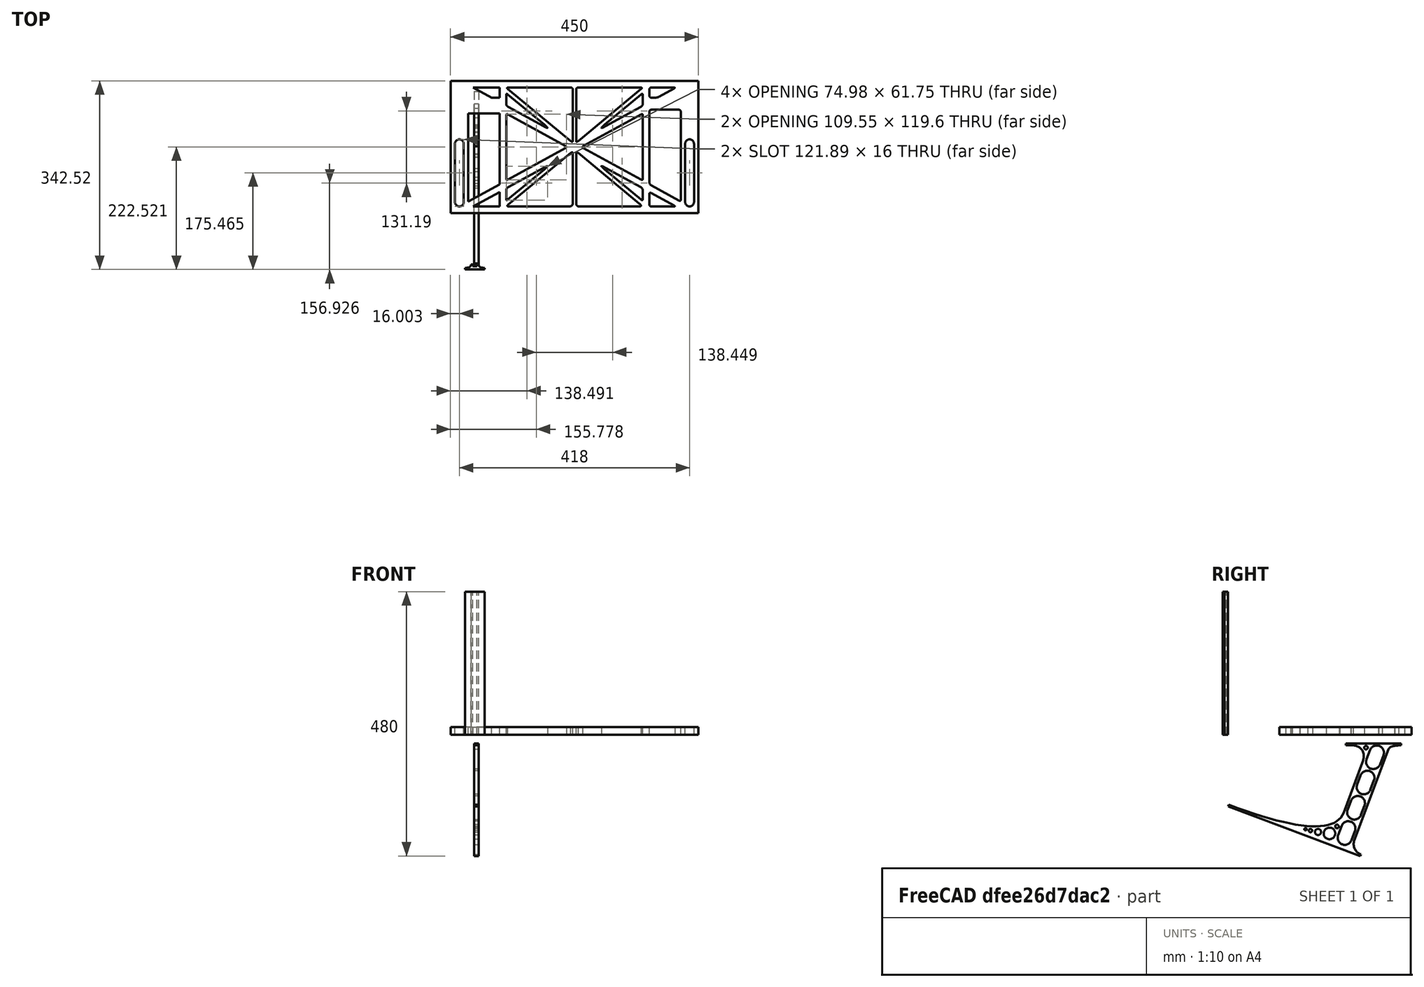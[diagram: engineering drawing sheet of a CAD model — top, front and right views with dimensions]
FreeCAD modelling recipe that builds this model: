
FCSTD DOCUMENT  (FreeCAD 0.19R0.19.2)
Label: laptopStand113
License: All rights reserved
LicenseURL: http://en.wikipedia.org/wiki/All_rights_reserved
objects: Sketcher::SketchObject×3, Part::Extrusion×3
note: 6 computed .brp shape members not serialized (recipe doc carries the construction recipe); baked Part::Feature solids carry a one-line shape summary decoded from their .brp

FEATURE [Sketcher::SketchObject] Sketch
  FullyConstrained = true
  sketch-geometry (310):
    g0: LineSegment StartX=-10.9272 StartY=-82.7794 StartZ=0 EndX=46.0728 EndY=-51.4823 EndZ=0
    g1: LineSegment StartX=-10.9272 StartY=77.3346 StartZ=0 EndX=-10.9272 EndY=-82.7794 EndZ=0
    g2: LineSegment StartX=-1.92719 StartY=-91.7794 StartZ=0 EndX=46.0728 EndY=-91.7794 EndZ=0
    g3: LineSegment StartX=46.0728 StartY=-65.424 StartZ=0 EndX=-1.92719 EndY=-91.7794 EndZ=0
    g4: LineSegment StartX=46.0728 StartY=-65.424 StartZ=0 EndX=46.0728 EndY=-91.7794 EndZ=0
    g5: LineSegment StartX=46.0728 StartY=77.3346 StartZ=0 EndX=46.0728 EndY=-51.4823 EndZ=0
    g6: LineSegment StartX=-42.9272 StartY=136.221 StartZ=0 EndX=-42.9272 EndY=-103.779 EndZ=0
    g7: LineSegment StartX=407.073 StartY=136.221 StartZ=0 EndX=407.073 EndY=-103.779 EndZ=0
    g8: ArcOfCircle CenterX=-26.9272 CenterY=22.1087 CenterZ=0 NormalX=0 NormalY=0 NormalZ=1 AngleXU=0 Radius=8 StartAngle=1e-16 EndAngle=3.14159
    g9: ArcOfCircle CenterX=-26.9272 CenterY=-83.7794 CenterZ=0 NormalX=0 NormalY=0 NormalZ=1 AngleXU=0 Radius=8 StartAngle=3.14159 EndAngle=6.28319
    g10: LineSegment StartX=-34.9272 StartY=22.1087 StartZ=0 EndX=-34.9272 EndY=-83.7794 EndZ=0
    g11: LineSegment StartX=-18.9272 StartY=22.1087 StartZ=0 EndX=-18.9272 EndY=-83.7794 EndZ=0
    g12: ArcOfCircle CenterX=391.073 CenterY=22.1087 CenterZ=0 NormalX=0 NormalY=0 NormalZ=1 AngleXU=0 Radius=8 StartAngle=-4.4e-15 EndAngle=3.14159
    g13: LineSegment StartX=399.073 StartY=22.1087 StartZ=0 EndX=399.073 EndY=-83.7794 EndZ=0
    g14: LineSegment StartX=383.073 StartY=22.1087 StartZ=0 EndX=383.073 EndY=-83.7794 EndZ=0
    g15: ArcOfCircle CenterX=391.073 CenterY=-83.7794 CenterZ=0 NormalX=0 NormalY=0 NormalZ=1 AngleXU=0 Radius=8 StartAngle=3.14159 EndAngle=6.28319
    g16: Circle CenterX=175.022 CenterY=27.0628 CenterZ=0 NormalX=0 NormalY=0 NormalZ=1 AngleXU=0 Radius=1
    g17: Circle CenterX=179.022 CenterY=24.8665 CenterZ=0 NormalX=0 NormalY=0 NormalZ=1 AngleXU=0 Radius=1
    g18: Circle CenterX=179.022 CenterY=27.0628 CenterZ=0 NormalX=0 NormalY=0 NormalZ=1 AngleXU=0 Radius=1
    g19: BSplineCurve PolesCount=3 KnotsCount=2 Degree=2 IsPeriodic=0
    g20: GeomPoint X=175.022 Y=27.0628 Z=0
    g21: GeomPoint X=179.022 Y=27.0628 Z=0
    g22: Circle CenterX=189.124 CenterY=27.0628 CenterZ=0 NormalX=0 NormalY=0 NormalZ=1 AngleXU=0 Radius=1
    g23: Circle CenterX=185.124 CenterY=24.8665 CenterZ=0 NormalX=0 NormalY=0 NormalZ=1 AngleXU=0 Radius=1
    g24: Circle CenterX=185.124 CenterY=27.0628 CenterZ=0 NormalX=0 NormalY=0 NormalZ=1 AngleXU=0 Radius=1
    g25: BSplineCurve PolesCount=3 KnotsCount=2 Degree=2 IsPeriodic=0
    g26: GeomPoint X=189.124 Y=27.0628 Z=0
    g27: GeomPoint X=185.124 Y=27.0628 Z=0
    g28: Circle CenterX=175.022 CenterY=5.37834 CenterZ=0 NormalX=0 NormalY=0 NormalZ=1 AngleXU=0 Radius=1
    g29: Circle CenterX=179.022 CenterY=7.57463 CenterZ=0 NormalX=0 NormalY=0 NormalZ=1 AngleXU=0 Radius=1
    g30: Circle CenterX=179.022 CenterY=5.34704 CenterZ=0 NormalX=0 NormalY=0 NormalZ=1 AngleXU=0 Radius=1
    g31: BSplineCurve PolesCount=3 KnotsCount=2 Degree=2 IsPeriodic=0
    g32: GeomPoint X=175.022 Y=5.37834 Z=0
    g33: GeomPoint X=179.022 Y=5.34704 Z=0
    g34: Circle CenterX=189.124 CenterY=5.37834 CenterZ=0 NormalX=0 NormalY=0 NormalZ=1 AngleXU=0 Radius=1
    g35: Circle CenterX=185.124 CenterY=7.57463 CenterZ=0 NormalX=0 NormalY=0 NormalZ=1 AngleXU=0 Radius=1
    g36: Circle CenterX=185.124 CenterY=5.34704 CenterZ=0 NormalX=0 NormalY=0 NormalZ=1 AngleXU=0 Radius=1
    g37: BSplineCurve PolesCount=3 KnotsCount=2 Degree=2 IsPeriodic=0
    g38: GeomPoint X=189.124 Y=5.37834 Z=0
    g39: GeomPoint X=185.124 Y=5.34704 Z=0
    g40: Circle CenterX=165.871 CenterY=18.1458 CenterZ=0 NormalX=0 NormalY=0 NormalZ=1 AngleXU=0 Radius=1
    g41: Circle CenterX=169.377 CenterY=16.2206 CenterZ=0 NormalX=0 NormalY=0 NormalZ=1 AngleXU=0 Radius=1
    g42: Circle CenterX=165.871 CenterY=14.2954 CenterZ=0 NormalX=0 NormalY=0 NormalZ=1 AngleXU=0 Radius=1
    g43: BSplineCurve PolesCount=3 KnotsCount=2 Degree=2 IsPeriodic=0
    g44: GeomPoint X=165.871 Y=18.1458 Z=0
    g45: GeomPoint X=165.871 Y=14.2954 Z=0
    g46: Circle CenterX=198.275 CenterY=18.1458 CenterZ=0 NormalX=0 NormalY=0 NormalZ=1 AngleXU=0 Radius=1
    g47: Circle CenterX=194.768 CenterY=16.2206 CenterZ=0 NormalX=0 NormalY=0 NormalZ=1 AngleXU=0 Radius=1
    g48: Circle CenterX=198.275 CenterY=14.2954 CenterZ=0 NormalX=0 NormalY=0 NormalZ=1 AngleXU=0 Radius=1
    g49: BSplineCurve PolesCount=3 KnotsCount=2 Degree=2 IsPeriodic=0
    g50: GeomPoint X=198.275 Y=18.1458 Z=0
    g51: GeomPoint X=198.275 Y=14.2954 Z=0
    g52: LineSegment StartX=407.073 StartY=-103.779 StartZ=0 EndX=-42.9272 EndY=-103.779 EndZ=0
    g53: LineSegment StartX=407.073 StartY=136.221 StartZ=0 EndX=-42.9272 EndY=136.221 EndZ=0
    g54: LineSegment StartX=46.0728 StartY=77.3346 StartZ=0 EndX=-10.9272 EndY=77.3346 EndZ=0
    g55: LineSegment StartX=46.0728 StartY=105.865 StartZ=0 EndX=31.5028 EndY=105.865 EndZ=0
    g56: LineSegment StartX=46.0728 StartY=124.221 StartZ=0 EndX=46.0728 EndY=105.865 EndZ=0
    g57: LineSegment StartX=-1.92719 StartY=124.221 StartZ=0 EndX=31.5028 EndY=105.865 EndZ=0
    g58: LineSegment StartX=46.0728 StartY=124.221 StartZ=0 EndX=-1.92719 EndY=124.221 EndZ=0
    g59: Circle CenterX=125.607 CenterY=54.1951 CenterZ=0 NormalX=0 NormalY=0 NormalZ=1 AngleXU=0 Radius=1
    g60: Circle CenterX=139.632 CenterY=46.4944 CenterZ=0 NormalX=0 NormalY=0 NormalZ=1 AngleXU=0 Radius=1
    g61: Circle CenterX=127.326 CenterY=56.7187 CenterZ=0 NormalX=0 NormalY=0 NormalZ=1 AngleXU=0 Radius=1
    g62: BSplineCurve PolesCount=3 KnotsCount=2 Degree=2 IsPeriodic=0
    g63: GeomPoint X=125.607 Y=54.1951 Z=0
    g64: GeomPoint X=127.326 Y=56.7187 Z=0
    g65: Circle CenterX=236.821 CenterY=56.7187 CenterZ=0 NormalX=0 NormalY=0 NormalZ=1 AngleXU=0 Radius=1
    g66: Circle CenterX=224.513 CenterY=46.4944 CenterZ=0 NormalX=0 NormalY=0 NormalZ=1 AngleXU=0 Radius=1
    g67: Circle CenterX=238.538 CenterY=54.1951 CenterZ=0 NormalX=0 NormalY=0 NormalZ=1 AngleXU=0 Radius=1
    g68: BSplineCurve PolesCount=3 KnotsCount=2 Degree=2 IsPeriodic=0
    g69: GeomPoint X=236.821 Y=56.7187 Z=0
    g70: GeomPoint X=238.538 Y=54.1951 Z=0
    g71: Circle CenterX=238.538 CenterY=-21.7539 CenterZ=0 NormalX=0 NormalY=0 NormalZ=1 AngleXU=0 Radius=1
    g72: Circle CenterX=224.513 CenterY=-14.0532 CenterZ=0 NormalX=0 NormalY=0 NormalZ=1 AngleXU=0 Radius=1
    g73: Circle CenterX=236.821 CenterY=-24.2775 CenterZ=0 NormalX=0 NormalY=0 NormalZ=1 AngleXU=0 Radius=1
    g74: BSplineCurve PolesCount=3 KnotsCount=2 Degree=2 IsPeriodic=0
    g75: GeomPoint X=238.538 Y=-21.7539 Z=0
    g76: GeomPoint X=236.821 Y=-24.2775 Z=0
    g77: Circle CenterX=125.607 CenterY=-21.7539 CenterZ=0 NormalX=0 NormalY=0 NormalZ=1 AngleXU=0 Radius=1
    g78: Circle CenterX=139.632 CenterY=-14.0532 CenterZ=0 NormalX=0 NormalY=0 NormalZ=1 AngleXU=0 Radius=1
    g79: Circle CenterX=127.325 CenterY=-24.2775 CenterZ=0 NormalX=0 NormalY=0 NormalZ=1 AngleXU=0 Radius=1
    g80: BSplineCurve PolesCount=3 KnotsCount=2 Degree=2 IsPeriodic=0
    g81: GeomPoint X=125.607 Y=-21.7539 Z=0
    g82: GeomPoint X=127.325 Y=-24.2775 Z=0
    g83: Circle CenterX=302.996 CenterY=111.695 CenterZ=0 NormalX=0 NormalY=0 NormalZ=1 AngleXU=0 Radius=1
    g84: Circle CenterX=306.073 CenterY=114.251 CenterZ=0 NormalX=0 NormalY=0 NormalZ=1 AngleXU=0 Radius=1
    g85: Circle CenterX=306.073 CenterY=110.251 CenterZ=0 NormalX=0 NormalY=0 NormalZ=1 AngleXU=0 Radius=1
    g86: BSplineCurve PolesCount=3 KnotsCount=2 Degree=2 IsPeriodic=0
    g87: GeomPoint X=302.996 Y=111.695 Z=0
    g88: GeomPoint X=306.073 Y=110.251 Z=0
    g89: Circle CenterX=306.073 CenterY=95.2763 CenterZ=0 NormalX=0 NormalY=0 NormalZ=1 AngleXU=0 Radius=1
    g90: Circle CenterX=306.073 CenterY=91.2763 CenterZ=0 NormalX=0 NormalY=0 NormalZ=1 AngleXU=0 Radius=1
    g91: Circle CenterX=302.567 CenterY=89.3511 CenterZ=0 NormalX=0 NormalY=0 NormalZ=1 AngleXU=0 Radius=1
    g92: BSplineCurve PolesCount=3 KnotsCount=2 Degree=2 IsPeriodic=0
    g93: GeomPoint X=306.073 Y=95.2763 Z=0
    g94: GeomPoint X=302.567 Y=89.3511 Z=0
    g95: LineSegment StartX=306.073 StartY=110.251 StartZ=0 EndX=306.073 EndY=95.2763 EndZ=0
    g96: LineSegment StartX=302.996 StartY=111.695 StartZ=0 EndX=236.821 EndY=56.7187 EndZ=0
    g97: LineSegment StartX=238.538 StartY=54.1951 StartZ=0 EndX=302.567 EndY=89.3511 EndZ=0
    g98: Circle CenterX=61.1496 CenterY=111.695 CenterZ=0 NormalX=0 NormalY=0 NormalZ=1 AngleXU=0 Radius=1
    g99: Circle CenterX=58.0728 CenterY=114.251 CenterZ=0 NormalX=0 NormalY=0 NormalZ=1 AngleXU=0 Radius=1
    g100: Circle CenterX=58.0728 CenterY=110.251 CenterZ=0 NormalX=0 NormalY=0 NormalZ=1 AngleXU=0 Radius=1
    g101: BSplineCurve PolesCount=3 KnotsCount=2 Degree=2 IsPeriodic=0
    g102: GeomPoint X=61.1496 Y=111.695 Z=0
    g103: GeomPoint X=58.0728 Y=110.251 Z=0
    g104: Circle CenterX=61.5791 CenterY=89.3511 CenterZ=0 NormalX=0 NormalY=0 NormalZ=1 AngleXU=0 Radius=1
    g105: Circle CenterX=58.0728 CenterY=91.2763 CenterZ=0 NormalX=0 NormalY=0 NormalZ=1 AngleXU=0 Radius=1
    g106: Circle CenterX=58.0728 CenterY=95.2763 CenterZ=0 NormalX=0 NormalY=0 NormalZ=1 AngleXU=0 Radius=1
    g107: BSplineCurve PolesCount=3 KnotsCount=2 Degree=2 IsPeriodic=0
    g108: GeomPoint X=61.5791 Y=89.3511 Z=0
    g109: GeomPoint X=58.0728 Y=95.2763 Z=0
    g110: LineSegment StartX=58.0728 StartY=110.251 StartZ=0 EndX=58.0728 EndY=95.2763 EndZ=0
    g111: LineSegment StartX=61.1496 StartY=111.695 StartZ=0 EndX=127.326 EndY=56.7187 EndZ=0
    g112: LineSegment StartX=125.607 StartY=54.1951 StartZ=0 EndX=61.5791 EndY=89.3511 EndZ=0
    g113: Circle CenterX=61.5791 CenterY=-56.9099 CenterZ=0 NormalX=0 NormalY=0 NormalZ=1 AngleXU=0 Radius=1
    g114: Circle CenterX=58.0728 CenterY=-58.8351 CenterZ=0 NormalX=0 NormalY=0 NormalZ=1 AngleXU=0 Radius=1
    g115: Circle CenterX=58.0728 CenterY=-62.8351 CenterZ=0 NormalX=0 NormalY=0 NormalZ=1 AngleXU=0 Radius=1
    g116: BSplineCurve PolesCount=3 KnotsCount=2 Degree=2 IsPeriodic=0
    g117: GeomPoint X=61.5791 Y=-56.9099 Z=0
    g118: GeomPoint X=58.0728 Y=-62.8351 Z=0
    g119: Circle CenterX=58.0728 CenterY=-77.8102 CenterZ=0 NormalX=0 NormalY=0 NormalZ=1 AngleXU=0 Radius=1
    g120: Circle CenterX=58.0728 CenterY=-81.8102 CenterZ=0 NormalX=0 NormalY=0 NormalZ=1 AngleXU=0 Radius=1
    g121: Circle CenterX=61.1496 CenterY=-79.2541 CenterZ=0 NormalX=0 NormalY=0 NormalZ=1 AngleXU=0 Radius=1
    g122: BSplineCurve PolesCount=3 KnotsCount=2 Degree=2 IsPeriodic=0
    g123: GeomPoint X=58.0728 Y=-77.8102 Z=0
    g124: GeomPoint X=61.1496 Y=-79.2541 Z=0
    g125: LineSegment StartX=58.0728 StartY=-62.8351 StartZ=0 EndX=58.0728 EndY=-77.8102 EndZ=0
    g126: LineSegment StartX=61.1496 StartY=-79.2541 StartZ=0 EndX=127.325 EndY=-24.2775 EndZ=0
    g127: LineSegment StartX=125.607 StartY=-21.7539 StartZ=0 EndX=61.5791 EndY=-56.9099 EndZ=0
    g128: Circle CenterX=302.567 CenterY=-56.9099 CenterZ=0 NormalX=0 NormalY=0 NormalZ=1 AngleXU=0 Radius=1
    g129: Circle CenterX=306.073 CenterY=-58.8351 CenterZ=0 NormalX=0 NormalY=0 NormalZ=1 AngleXU=0 Radius=1
    g130: Circle CenterX=306.073 CenterY=-62.8351 CenterZ=0 NormalX=0 NormalY=0 NormalZ=1 AngleXU=0 Radius=1
    g131: BSplineCurve PolesCount=3 KnotsCount=2 Degree=2 IsPeriodic=0
    g132: GeomPoint X=302.567 Y=-56.9099 Z=0
    g133: GeomPoint X=306.073 Y=-62.8351 Z=0
    g134: Circle CenterX=302.996 CenterY=-79.2541 CenterZ=0 NormalX=0 NormalY=0 NormalZ=1 AngleXU=0 Radius=1
    g135: Circle CenterX=306.073 CenterY=-81.8102 CenterZ=0 NormalX=0 NormalY=0 NormalZ=1 AngleXU=0 Radius=1
    g136: Circle CenterX=306.073 CenterY=-77.8102 CenterZ=0 NormalX=0 NormalY=0 NormalZ=1 AngleXU=0 Radius=1
    g137: BSplineCurve PolesCount=3 KnotsCount=2 Degree=2 IsPeriodic=0
    g138: GeomPoint X=302.996 Y=-79.2541 Z=0
    g139: GeomPoint X=306.073 Y=-77.8102 Z=0
    g140: LineSegment StartX=306.073 StartY=-62.8351 StartZ=0 EndX=306.073 EndY=-77.8102 EndZ=0
    g141: LineSegment StartX=302.996 StartY=-79.2541 StartZ=0 EndX=236.821 EndY=-24.2775 EndZ=0
    g142: LineSegment StartX=238.538 StartY=-21.7539 StartZ=0 EndX=302.567 EndY=-56.9099 EndZ=0
    g143: Circle CenterX=61.6457 CenterY=-88.8112 CenterZ=0 NormalX=0 NormalY=0 NormalZ=1 AngleXU=0 Radius=1
    g144: Circle CenterX=58.0728 CenterY=-91.7794 CenterZ=0 NormalX=0 NormalY=0 NormalZ=1 AngleXU=0 Radius=1
    g145: Circle CenterX=63.9135 CenterY=-91.7794 CenterZ=0 NormalX=0 NormalY=0 NormalZ=1 AngleXU=0 Radius=1
    g146: BSplineCurve PolesCount=3 KnotsCount=2 Degree=2 IsPeriodic=0
    g147: GeomPoint X=61.6457 Y=-88.8112 Z=0
    g148: GeomPoint X=63.9135 Y=-91.7794 Z=0
    g149: Circle CenterX=179.022 CenterY=-85.8163 CenterZ=0 NormalX=0 NormalY=0 NormalZ=1 AngleXU=0 Radius=1
    g150: Circle CenterX=179.022 CenterY=-91.7794 CenterZ=0 NormalX=0 NormalY=0 NormalZ=1 AngleXU=0 Radius=1
    g151: Circle CenterX=171.895 CenterY=-91.7794 CenterZ=0 NormalX=0 NormalY=0 NormalZ=1 AngleXU=0 Radius=1
    g152: BSplineCurve PolesCount=3 KnotsCount=2 Degree=2 IsPeriodic=0
    g153: GeomPoint X=179.022 Y=-85.8163 Z=0
    g154: GeomPoint X=171.895 Y=-91.7794 Z=0
    g155: Circle CenterX=185.124 CenterY=-86.2028 CenterZ=0 NormalX=0 NormalY=0 NormalZ=1 AngleXU=0 Radius=1
    g156: Circle CenterX=185.124 CenterY=-91.7794 CenterZ=0 NormalX=0 NormalY=0 NormalZ=1 AngleXU=0 Radius=1
    g157: Circle CenterX=191.747 CenterY=-91.7794 CenterZ=0 NormalX=0 NormalY=0 NormalZ=1 AngleXU=0 Radius=1
    g158: BSplineCurve PolesCount=3 KnotsCount=2 Degree=2 IsPeriodic=0
    g159: GeomPoint X=185.124 Y=-86.2028 Z=0
    g160: GeomPoint X=191.747 Y=-91.7794 Z=0
    g161: Circle CenterX=299.888 CenterY=-86.6413 CenterZ=0 NormalX=0 NormalY=0 NormalZ=1 AngleXU=0 Radius=1
    g162: Circle CenterX=306.073 CenterY=-91.7794 CenterZ=0 NormalX=0 NormalY=0 NormalZ=1 AngleXU=0 Radius=1
    g163: Circle CenterX=298.776 CenterY=-91.7794 CenterZ=0 NormalX=0 NormalY=0 NormalZ=1 AngleXU=0 Radius=1
    g164: BSplineCurve PolesCount=3 KnotsCount=2 Degree=2 IsPeriodic=0
    g165: GeomPoint X=299.888 Y=-86.6413 Z=0
    g166: GeomPoint X=298.776 Y=-91.7794 Z=0
    g167: LineSegment StartX=189.124 StartY=5.37834 StartZ=0 EndX=299.888 EndY=-86.6413 EndZ=0
    g168: LineSegment StartX=298.776 StartY=-91.7794 StartZ=0 EndX=191.747 EndY=-91.7794 EndZ=0
    g169: LineSegment StartX=185.124 StartY=-86.2028 StartZ=0 EndX=185.124 EndY=5.34704 EndZ=0
    g170: LineSegment StartX=179.022 StartY=5.34704 StartZ=0 EndX=179.022 EndY=-85.8163 EndZ=0
    g171: LineSegment StartX=171.895 StartY=-91.7794 StartZ=0 EndX=63.9135 EndY=-91.7794 EndZ=0
    g172: LineSegment StartX=61.6457 StartY=-88.8112 StartZ=0 EndX=175.022 EndY=5.37834 EndZ=0
    g173: Circle CenterX=302.073 CenterY=124.221 CenterZ=0 NormalX=0 NormalY=0 NormalZ=1 AngleXU=0 Radius=1
    g174: Circle CenterX=306.073 CenterY=124.221 CenterZ=0 NormalX=0 NormalY=0 NormalZ=1 AngleXU=0 Radius=1
    g175: Circle CenterX=302.996 CenterY=121.665 CenterZ=0 NormalX=0 NormalY=0 NormalZ=1 AngleXU=0 Radius=1
    g176: BSplineCurve PolesCount=3 KnotsCount=2 Degree=2 IsPeriodic=0
    g177: GeomPoint X=302.073 Y=124.221 Z=0
    g178: GeomPoint X=302.996 Y=121.665 Z=0
    g179: Circle CenterX=189.124 CenterY=124.221 CenterZ=0 NormalX=0 NormalY=0 NormalZ=1 AngleXU=0 Radius=1
    g180: Circle CenterX=185.124 CenterY=124.221 CenterZ=0 NormalX=0 NormalY=0 NormalZ=1 AngleXU=0 Radius=1
    g181: Circle CenterX=185.124 CenterY=120.221 CenterZ=0 NormalX=0 NormalY=0 NormalZ=1 AngleXU=0 Radius=1
    g182: BSplineCurve PolesCount=3 KnotsCount=2 Degree=2 IsPeriodic=0
    g183: GeomPoint X=189.124 Y=124.221 Z=0
    g184: GeomPoint X=185.124 Y=120.221 Z=0
    g185: Circle CenterX=175.022 CenterY=124.221 CenterZ=0 NormalX=0 NormalY=0 NormalZ=1 AngleXU=0 Radius=1
    g186: Circle CenterX=179.022 CenterY=124.221 CenterZ=0 NormalX=0 NormalY=0 NormalZ=1 AngleXU=0 Radius=1
    g187: Circle CenterX=179.022 CenterY=120.221 CenterZ=0 NormalX=0 NormalY=0 NormalZ=1 AngleXU=0 Radius=1
    g188: BSplineCurve PolesCount=3 KnotsCount=2 Degree=2 IsPeriodic=0
    g189: GeomPoint X=175.022 Y=124.221 Z=0
    g190: GeomPoint X=179.022 Y=120.221 Z=0
    g191: Circle CenterX=62.0728 CenterY=124.221 CenterZ=0 NormalX=0 NormalY=0 NormalZ=1 AngleXU=0 Radius=1
    g192: Circle CenterX=58.0728 CenterY=124.221 CenterZ=0 NormalX=0 NormalY=0 NormalZ=1 AngleXU=0 Radius=1
    g193: Circle CenterX=61.1496 CenterY=121.665 CenterZ=0 NormalX=0 NormalY=0 NormalZ=1 AngleXU=0 Radius=1
    g194: BSplineCurve PolesCount=3 KnotsCount=2 Degree=2 IsPeriodic=0
    g195: GeomPoint X=62.0728 Y=124.221 Z=0
    g196: GeomPoint X=61.1496 Y=121.665 Z=0
    g197: LineSegment StartX=62.0728 StartY=124.221 StartZ=0 EndX=175.022 EndY=124.221 EndZ=0
    g198: LineSegment StartX=179.022 StartY=120.221 StartZ=0 EndX=179.022 EndY=27.0628 EndZ=0
    g199: LineSegment StartX=185.124 StartY=27.0628 StartZ=0 EndX=185.124 EndY=120.221 EndZ=0
    g200: LineSegment StartX=189.124 StartY=124.221 StartZ=0 EndX=302.073 EndY=124.221 EndZ=0
    g201: LineSegment StartX=302.996 StartY=121.665 StartZ=0 EndX=189.124 EndY=27.0628 EndZ=0
    g202: LineSegment StartX=175.022 StartY=27.0628 StartZ=0 EndX=61.1496 EndY=121.665 EndZ=0
    g203: Circle CenterX=61.5791 CenterY=75.4095 CenterZ=0 NormalX=0 NormalY=0 NormalZ=1 AngleXU=0 Radius=1
    g204: Circle CenterX=58.0728 CenterY=77.3346 CenterZ=0 NormalX=0 NormalY=0 NormalZ=1 AngleXU=0 Radius=1
    g205: Circle CenterX=58.0728 CenterY=73.3346 CenterZ=0 NormalX=0 NormalY=0 NormalZ=1 AngleXU=0 Radius=1
    g206: BSplineCurve PolesCount=3 KnotsCount=2 Degree=2 IsPeriodic=0
    g207: GeomPoint X=61.5791 Y=75.4095 Z=0
    g208: GeomPoint X=58.0728 Y=73.3346 Z=0
    g209: Circle CenterX=58.0728 CenterY=-40.8935 CenterZ=0 NormalX=0 NormalY=0 NormalZ=1 AngleXU=0 Radius=1
    g210: Circle CenterX=58.0728 CenterY=-44.8935 CenterZ=0 NormalX=0 NormalY=0 NormalZ=1 AngleXU=0 Radius=1
    g211: Circle CenterX=61.5791 CenterY=-42.9683 CenterZ=0 NormalX=0 NormalY=0 NormalZ=1 AngleXU=0 Radius=1
    g212: BSplineCurve PolesCount=3 KnotsCount=2 Degree=2 IsPeriodic=0
    g213: GeomPoint X=58.0728 Y=-40.8935 Z=0
    g214: GeomPoint X=61.5791 Y=-42.9683 Z=0
    g215: LineSegment StartX=61.5791 StartY=-42.9683 StartZ=0 EndX=165.871 EndY=14.2954 EndZ=0
    g216: LineSegment StartX=165.871 StartY=18.1458 StartZ=0 EndX=61.5791 EndY=75.4095 EndZ=0
    g217: LineSegment StartX=58.0728 StartY=73.3346 StartZ=0 EndX=58.0728 EndY=-40.8935 EndZ=0
    g218: Circle CenterX=302.567 CenterY=-42.9683 CenterZ=0 NormalX=0 NormalY=0 NormalZ=1 AngleXU=0 Radius=1
    g219: Circle CenterX=306.073 CenterY=-44.8935 CenterZ=0 NormalX=0 NormalY=0 NormalZ=1 AngleXU=0 Radius=1
    g220: Circle CenterX=306.073 CenterY=-40.8935 CenterZ=0 NormalX=0 NormalY=0 NormalZ=1 AngleXU=0 Radius=1
    g221: BSplineCurve PolesCount=3 KnotsCount=2 Degree=2 IsPeriodic=0
    g222: GeomPoint X=302.567 Y=-42.9683 Z=0
    g223: GeomPoint X=306.073 Y=-40.8935 Z=0
    g224: Circle CenterX=306.073 CenterY=73.3346 CenterZ=0 NormalX=0 NormalY=0 NormalZ=1 AngleXU=0 Radius=1
    g225: Circle CenterX=306.073 CenterY=77.3346 CenterZ=0 NormalX=0 NormalY=0 NormalZ=1 AngleXU=0 Radius=1
    g226: Circle CenterX=302.567 CenterY=75.4095 CenterZ=0 NormalX=0 NormalY=0 NormalZ=1 AngleXU=0 Radius=1
    g227: BSplineCurve PolesCount=3 KnotsCount=2 Degree=2 IsPeriodic=0
    g228: GeomPoint X=306.073 Y=73.3346 Z=0
    g229: GeomPoint X=302.567 Y=75.4095 Z=0
    g230: LineSegment StartX=302.567 StartY=-42.9683 StartZ=0 EndX=198.275 EndY=14.2954 EndZ=0
    g231: LineSegment StartX=198.275 StartY=18.1458 StartZ=0 EndX=302.567 EndY=75.4095 EndZ=0
    g232: LineSegment StartX=306.073 StartY=73.3346 StartZ=0 EndX=306.073 EndY=-40.8935 EndZ=0
    g233: LineSegment StartX=322.073 StartY=105.865 StartZ=0 EndX=328.643 EndY=105.865 EndZ=0
    g234: LineSegment StartX=318.073 StartY=120.221 StartZ=0 EndX=318.073 EndY=109.865 EndZ=0
    g235: LineSegment StartX=336.157 StartY=107.779 StartZ=0 EndX=362.567 EndY=122.294 EndZ=0
    g236: Circle CenterX=362.073 CenterY=124.221 CenterZ=0 NormalX=0 NormalY=0 NormalZ=1 AngleXU=0 Radius=1
    g237: Circle CenterX=366.073 CenterY=124.221 CenterZ=0 NormalX=0 NormalY=0 NormalZ=1 AngleXU=0 Radius=1
    g238: Circle CenterX=362.567 CenterY=122.294 CenterZ=0 NormalX=0 NormalY=0 NormalZ=1 AngleXU=0 Radius=1
    g239: BSplineCurve PolesCount=3 KnotsCount=2 Degree=2 IsPeriodic=0
    g240: GeomPoint X=362.073 Y=124.221 Z=0
    g241: GeomPoint X=362.567 Y=122.294 Z=0
    g242: Circle CenterX=322.073 CenterY=124.221 CenterZ=0 NormalX=0 NormalY=0 NormalZ=1 AngleXU=0 Radius=1
    g243: Circle CenterX=318.073 CenterY=124.221 CenterZ=0 NormalX=0 NormalY=0 NormalZ=1 AngleXU=0 Radius=1
    g244: Circle CenterX=318.073 CenterY=120.221 CenterZ=0 NormalX=0 NormalY=0 NormalZ=1 AngleXU=0 Radius=1
    g245: BSplineCurve PolesCount=3 KnotsCount=2 Degree=2 IsPeriodic=0
    g246: GeomPoint X=322.073 Y=124.221 Z=0
    g247: GeomPoint X=318.073 Y=120.221 Z=0
    g248: Circle CenterX=322.073 CenterY=105.865 CenterZ=0 NormalX=0 NormalY=0 NormalZ=1 AngleXU=0 Radius=1
    g249: Circle CenterX=318.073 CenterY=105.865 CenterZ=0 NormalX=0 NormalY=0 NormalZ=1 AngleXU=0 Radius=1
    g250: Circle CenterX=318.073 CenterY=109.865 CenterZ=0 NormalX=0 NormalY=0 NormalZ=1 AngleXU=0 Radius=1
    g251: BSplineCurve PolesCount=3 KnotsCount=2 Degree=2 IsPeriodic=0
    g252: GeomPoint X=322.073 Y=105.865 Z=0
    g253: GeomPoint X=318.073 Y=109.865 Z=0
    g254: Circle CenterX=336.157 CenterY=107.779 CenterZ=0 NormalX=0 NormalY=0 NormalZ=1 AngleXU=0 Radius=1
    g255: Circle CenterX=332.651 CenterY=105.853 CenterZ=0 NormalX=0 NormalY=0 NormalZ=1 AngleXU=0 Radius=1
    g256: Circle CenterX=328.643 CenterY=105.865 CenterZ=0 NormalX=0 NormalY=0 NormalZ=1 AngleXU=0 Radius=1
    g257: BSplineCurve PolesCount=3 KnotsCount=2 Degree=2 IsPeriodic=0
    g258: GeomPoint X=336.157 Y=107.779 Z=0
    g259: GeomPoint X=328.643 Y=105.865 Z=0
    g260: LineSegment StartX=322.073 StartY=124.221 StartZ=0 EndX=362.073 EndY=124.221 EndZ=0
    g261: Circle CenterX=371.567 CenterY=-80.8644 CenterZ=0 NormalX=0 NormalY=0 NormalZ=1 AngleXU=0 Radius=1
    g262: Circle CenterX=375.073 CenterY=-82.7896 CenterZ=0 NormalX=0 NormalY=0 NormalZ=1 AngleXU=0 Radius=1
    g263: Circle CenterX=375.073 CenterY=-78.7896 CenterZ=0 NormalX=0 NormalY=0 NormalZ=1 AngleXU=0 Radius=1
    g264: BSplineCurve PolesCount=3 KnotsCount=2 Degree=2 IsPeriodic=0
    g265: GeomPoint X=371.567 Y=-80.8644 Z=0
    g266: GeomPoint X=375.073 Y=-78.7896 Z=0
    g267: Circle CenterX=321.579 CenterY=-53.4075 CenterZ=0 NormalX=0 NormalY=0 NormalZ=1 AngleXU=0 Radius=1
    g268: Circle CenterX=318.073 CenterY=-51.4823 CenterZ=0 NormalX=0 NormalY=0 NormalZ=1 AngleXU=0 Radius=1
    g269: Circle CenterX=318.073 CenterY=-47.4823 CenterZ=0 NormalX=0 NormalY=0 NormalZ=1 AngleXU=0 Radius=1
    g270: BSplineCurve PolesCount=3 KnotsCount=2 Degree=2 IsPeriodic=0
    g271: GeomPoint X=321.579 Y=-53.4075 Z=0
    g272: GeomPoint X=318.073 Y=-47.4823 Z=0
    g273: Circle CenterX=318.073 CenterY=79.9235 CenterZ=0 NormalX=0 NormalY=0 NormalZ=1 AngleXU=0 Radius=1
    g274: Circle CenterX=318.073 CenterY=83.9235 CenterZ=0 NormalX=0 NormalY=0 NormalZ=1 AngleXU=0 Radius=1
    g275: Circle CenterX=322.073 CenterY=83.9235 CenterZ=0 NormalX=0 NormalY=0 NormalZ=1 AngleXU=0 Radius=1
    g276: BSplineCurve PolesCount=3 KnotsCount=2 Degree=2 IsPeriodic=0
    g277: GeomPoint X=318.073 Y=79.9235 Z=0
    g278: GeomPoint X=322.073 Y=83.9235 Z=0
    g279: Circle CenterX=375.073 CenterY=79.9235 CenterZ=0 NormalX=0 NormalY=0 NormalZ=1 AngleXU=0 Radius=1
    g280: Circle CenterX=375.073 CenterY=83.9235 CenterZ=0 NormalX=0 NormalY=0 NormalZ=1 AngleXU=0 Radius=1
    g281: Circle CenterX=371.073 CenterY=83.9235 CenterZ=0 NormalX=0 NormalY=0 NormalZ=1 AngleXU=0 Radius=1
    g282: BSplineCurve PolesCount=3 KnotsCount=2 Degree=2 IsPeriodic=0
    g283: GeomPoint X=375.073 Y=79.9235 Z=0
    g284: GeomPoint X=371.073 Y=83.9235 Z=0
    g285: LineSegment StartX=322.073 StartY=83.9235 StartZ=0 EndX=371.073 EndY=83.9235 EndZ=0
    g286: LineSegment StartX=375.073 StartY=79.9235 StartZ=0 EndX=375.073 EndY=-78.7896 EndZ=0
    g287: LineSegment StartX=371.567 StartY=-80.8644 StartZ=0 EndX=321.579 EndY=-53.4075 EndZ=0
    g288: LineSegment StartX=318.073 StartY=-47.4823 StartZ=0 EndX=318.073 EndY=79.9235 EndZ=0
    g289: Circle CenterX=321.579 CenterY=-67.3492 CenterZ=0 NormalX=0 NormalY=0 NormalZ=1 AngleXU=0 Radius=1
    g290: Circle CenterX=318.073 CenterY=-65.424 CenterZ=0 NormalX=0 NormalY=0 NormalZ=1 AngleXU=0 Radius=1
    g291: Circle CenterX=318.073 CenterY=-69.424 CenterZ=0 NormalX=0 NormalY=0 NormalZ=1 AngleXU=0 Radius=1
    g292: BSplineCurve PolesCount=3 KnotsCount=2 Degree=2 IsPeriodic=0
    g293: GeomPoint X=321.579 Y=-67.3492 Z=0
    g294: GeomPoint X=318.073 Y=-69.424 Z=0
    g295: Circle CenterX=362.567 CenterY=-89.8542 CenterZ=0 NormalX=0 NormalY=0 NormalZ=1 AngleXU=0 Radius=1
    g296: Circle CenterX=366.073 CenterY=-91.7794 CenterZ=0 NormalX=0 NormalY=0 NormalZ=1 AngleXU=0 Radius=1
    g297: Circle CenterX=362.073 CenterY=-91.7794 CenterZ=0 NormalX=0 NormalY=0 NormalZ=1 AngleXU=0 Radius=1
    g298: BSplineCurve PolesCount=3 KnotsCount=2 Degree=2 IsPeriodic=0
    g299: GeomPoint X=362.567 Y=-89.8542 Z=0
    g300: GeomPoint X=362.073 Y=-91.7794 Z=0
    g301: Circle CenterX=322.073 CenterY=-91.7794 CenterZ=0 NormalX=0 NormalY=0 NormalZ=1 AngleXU=0 Radius=1
    g302: Circle CenterX=318.073 CenterY=-91.7794 CenterZ=0 NormalX=0 NormalY=0 NormalZ=1 AngleXU=0 Radius=1
    g303: Circle CenterX=318.073 CenterY=-87.7794 CenterZ=0 NormalX=0 NormalY=0 NormalZ=1 AngleXU=0 Radius=1
    g304: BSplineCurve PolesCount=3 KnotsCount=2 Degree=2 IsPeriodic=0
    g305: GeomPoint X=322.073 Y=-91.7794 Z=0
    g306: GeomPoint X=318.073 Y=-87.7794 Z=0
    g307: LineSegment StartX=362.567 StartY=-89.8542 StartZ=0 EndX=321.579 EndY=-67.3492 EndZ=0
    g308: LineSegment StartX=318.073 StartY=-69.424 StartZ=0 EndX=318.073 EndY=-87.7794 EndZ=0
    g309: LineSegment StartX=322.073 StartY=-91.7794 StartZ=0 EndX=362.073 EndY=-91.7794 EndZ=0
  constraints (519):
    c: Horizontal(g2)
    c: Coincident(g4,g3)
    c: Coincident(g0,g5)
    c: Block(g4)
    c: Block(g3)
    c: Block(g0)
    c: Block(g1)
    c: Block(g2)
    c: Vertical(g6)
    c: Vertical(g7)
    c: Block(g7)
    c: Block(g6)
    c: Tangent(g8,g11) = 1.5708
    c: Tangent(g8,g10) = -1.5708
    c: Tangent(g10,g9) = -1.5708
    c: Tangent(g11,g9) = 1.5708
    c: Vertical(g10)
    c: Equal(g8,g9)
    c: Block(g11)
    c: Block(g10)
    c: Tangent(g12,g13) = 1.5708
    c: Tangent(g13,g15) = 1.5708
    c: Equal(g12,g15)
    c: Coincident(g14,g12)
    c: Coincident(g14,g15)
    c: Block(g13)
    c: Block(g14)
    c: Weight(g16) = 1
    c: Equal(g16,g17)
    c: Equal(g16,g18)
    c: InternalAlignment(g16,g19)
    c: InternalAlignment(g17,g19)
    c: InternalAlignment(g18,g19)
    c: InternalAlignment(g20,g19)
    c: InternalAlignment(g21,g19)
    c: Weight(g22) = 1
    c: Equal(g22,g23)
    c: Equal(g22,g24)
    c: InternalAlignment(g22,g25)
    c: InternalAlignment(g23,g25)
    c: InternalAlignment(g24,g25)
    c: InternalAlignment(g26,g25)
    c: InternalAlignment(g27,g25)
    c: Block(g25)
    c: Block(g19)
    c: Weight(g28) = 1
    c: Equal(g28,g29)
    c: Equal(g28,g30)
    c: InternalAlignment(g28,g31)
    c: InternalAlignment(g29,g31)
    c: InternalAlignment(g30,g31)
    c: InternalAlignment(g32,g31)
    c: InternalAlignment(g33,g31)
    c: Weight(g34) = 1
    c: Equal(g34,g35)
    c: Equal(g34,g36)
    c: InternalAlignment(g34,g37)
    c: InternalAlignment(g35,g37)
    c: InternalAlignment(g36,g37)
    c: InternalAlignment(g38,g37)
    c: InternalAlignment(g39,g37)
    c: Block(g37)
    c: Block(g31)
    c: Weight(g40) = 1
    c: Equal(g40,g41)
    c: Equal(g40,g42)
    c: InternalAlignment(g40,g43)
    c: InternalAlignment(g41,g43)
    c: InternalAlignment(g42,g43)
    c: InternalAlignment(g44,g43)
    c: InternalAlignment(g45,g43)
    c: Weight(g46) = 1
    c: Equal(g46,g47)
    c: Equal(g46,g48)
    c: InternalAlignment(g46,g49)
    c: InternalAlignment(g47,g49)
    c: InternalAlignment(g48,g49)
    c: InternalAlignment(g50,g49)
    c: InternalAlignment(g51,g49)
    c: Block(g43)
    c: Block(g49)
    c: Coincident(g52,g7)
    c: Coincident(g52,g6)
    c: Horizontal(g52)
    c: Distance(g52) = 450
    c: Coincident(g53,g7)
    c: Coincident(g53,g6)
    c: Horizontal(g53)
    c: Horizontal(g54)
    c: Coincident(g5,g54)
    c: Horizontal(g55)
    c: Vertical(g56)
    c: Block(g56)
    c: Block(g55)
    c: Block(g54)
    c: Distance(g56) = 18.3554
    c: Coincident(g58,g56)
    c: Coincident(g58,g57)
    c: Horizontal(g58)
    c: Block(g58)
    c: Block(g57)
    c: Coincident(g55,g57)
    c: Coincident(g1,g54)
    c: Weight(g59) = 1
    c: Equal(g59,g60)
    c: Equal(g59,g61)
    c: InternalAlignment(g59,g62)
    c: InternalAlignment(g60,g62)
    c: InternalAlignment(g61,g62)
    c: InternalAlignment(g63,g62)
    c: InternalAlignment(g64,g62)
    c: Block(g62)
    c: Weight(g65) = 1
    c: Equal(g65,g66)
    c: Equal(g65,g67)
    c: InternalAlignment(g65,g68)
    c: InternalAlignment(g66,g68)
    c: InternalAlignment(g67,g68)
    c: InternalAlignment(g69,g68)
    c: InternalAlignment(g70,g68)
    c: Block(g68)
    c: Weight(g71) = 1
    c: Equal(g71,g72)
    c: Equal(g71,g73)
    c: InternalAlignment(g71,g74)
    c: InternalAlignment(g72,g74)
    c: InternalAlignment(g73,g74)
    c: InternalAlignment(g75,g74)
    c: InternalAlignment(g76,g74)
    c: Block(g74)
    c: Weight(g77) = 1
    c: Equal(g77,g78)
    c: Equal(g77,g79)
    c: InternalAlignment(g77,g80)
    c: InternalAlignment(g78,g80)
    c: InternalAlignment(g79,g80)
    c: InternalAlignment(g81,g80)
    c: InternalAlignment(g82,g80)
    c: Block(g80)
    c: Weight(g83) = 1
    c: Equal(g83,g84)
    c: Equal(g83,g85)
    c: InternalAlignment(g83,g86)
    c: InternalAlignment(g84,g86)
    c: InternalAlignment(g85,g86)
    c: InternalAlignment(g87,g86)
    c: InternalAlignment(g88,g86)
    c: Weight(g89) = 1
    c: Equal(g89,g90)
    c: Equal(g89,g91)
    c: InternalAlignment(g89,g92)
    c: InternalAlignment(g90,g92)
    c: InternalAlignment(g91,g92)
    c: InternalAlignment(g93,g92)
    c: InternalAlignment(g94,g92)
    c: Block(g86)
    c: Block(g92)
    c: Coincident(g95,g86)
    c: Coincident(g95,g92)
    c: Vertical(g95)
    c: Coincident(g96,g86)
    c: Coincident(g96,g68)
    c: Coincident(g97,g68)
    c: Coincident(g97,g92)
    c: Weight(g98) = 1
    c: Equal(g98,g99)
    c: Equal(g98,g100)
    c: InternalAlignment(g98,g101)
    c: InternalAlignment(g99,g101)
    c: InternalAlignment(g100,g101)
    c: InternalAlignment(g102,g101)
    c: InternalAlignment(g103,g101)
    c: Weight(g104) = 1
    c: Equal(g104,g105)
    c: Equal(g104,g106)
    c: InternalAlignment(g104,g107)
    c: InternalAlignment(g105,g107)
    c: InternalAlignment(g106,g107)
    c: InternalAlignment(g108,g107)
    c: InternalAlignment(g109,g107)
    c: Block(g101)
    c: Block(g107)
    c: Coincident(g110,g101)
    c: Coincident(g110,g107)
    c: Vertical(g110)
    c: Coincident(g111,g101)
    c: Coincident(g111,g62)
    c: Coincident(g112,g62)
    c: Coincident(g112,g107)
    c: Weight(g113) = 1
    c: Equal(g113,g114)
    c: Equal(g113,g115)
    c: InternalAlignment(g113,g116)
    c: InternalAlignment(g114,g116)
    c: InternalAlignment(g115,g116)
    c: InternalAlignment(g117,g116)
    c: InternalAlignment(g118,g116)
    c: Weight(g119) = 1
    c: Equal(g119,g120)
    c: Equal(g119,g121)
    c: InternalAlignment(g119,g122)
    c: InternalAlignment(g120,g122)
    c: InternalAlignment(g121,g122)
    c: InternalAlignment(g123,g122)
    c: InternalAlignment(g124,g122)
    c: Block(g116)
    c: Block(g122)
    c: Coincident(g125,g116)
    c: Coincident(g125,g122)
    c: Vertical(g125)
    c: Coincident(g126,g122)
    c: Coincident(g126,g80)
    c: Coincident(g127,g80)
    c: Coincident(g127,g116)
    c: Weight(g128) = 1
    c: Equal(g128,g129)
    c: Equal(g128,g130)
    c: InternalAlignment(g128,g131)
    c: InternalAlignment(g129,g131)
    c: InternalAlignment(g130,g131)
    c: InternalAlignment(g132,g131)
    c: InternalAlignment(g133,g131)
    c: Weight(g134) = 1
    c: Equal(g134,g135)
    c: Equal(g134,g136)
    c: InternalAlignment(g134,g137)
    c: InternalAlignment(g135,g137)
    c: InternalAlignment(g136,g137)
    c: InternalAlignment(g138,g137)
    c: InternalAlignment(g139,g137)
    c: Block(g131)
    c: Block(g137)
    c: Coincident(g140,g131)
    c: Coincident(g140,g137)
    c: Vertical(g140)
    c: Coincident(g141,g137)
    c: Coincident(g141,g74)
    c: Coincident(g142,g74)
    c: Coincident(g142,g131)
    c: Weight(g143) = 1
    c: Equal(g143,g144)
    c: Equal(g143,g145)
    c: InternalAlignment(g143,g146)
    c: InternalAlignment(g144,g146)
    c: InternalAlignment(g145,g146)
    c: InternalAlignment(g147,g146)
    c: InternalAlignment(g148,g146)
    c: Weight(g149) = 1
    c: Equal(g149,g150)
    c: Equal(g149,g151)
    c: InternalAlignment(g149,g152)
    c: InternalAlignment(g150,g152)
    c: InternalAlignment(g151,g152)
    c: InternalAlignment(g153,g152)
    c: InternalAlignment(g154,g152)
    c: Weight(g155) = 1
    c: Equal(g155,g156)
    c: Equal(g155,g157)
    c: InternalAlignment(g155,g158)
    c: InternalAlignment(g156,g158)
    c: InternalAlignment(g157,g158)
    c: InternalAlignment(g159,g158)
    c: InternalAlignment(g160,g158)
    c: Weight(g161) = 1
    c: Equal(g161,g162)
    c: Equal(g161,g163)
    c: InternalAlignment(g161,g164)
    c: InternalAlignment(g162,g164)
    c: InternalAlignment(g163,g164)
    c: InternalAlignment(g165,g164)
    c: InternalAlignment(g166,g164)
    c: Block(g164)
    c: Block(g158)
    c: Block(g152)
    c: Block(g146)
    c: Coincident(g167,g37)
    c: Coincident(g167,g164)
    c: Coincident(g168,g164)
    c: Coincident(g168,g158)
    c: Horizontal(g168)
    c: Coincident(g169,g158)
    c: Coincident(g169,g37)
    c: Vertical(g169)
    c: Coincident(g170,g31)
    c: Coincident(g170,g152)
    c: Vertical(g170)
    c: Coincident(g171,g152)
    c: Coincident(g171,g146)
    c: Horizontal(g171)
    c: Coincident(g172,g146)
    c: Coincident(g172,g31)
    c: Weight(g173) = 1
    c: Equal(g173,g174)
    c: Equal(g173,g175)
    c: InternalAlignment(g173,g176)
    c: InternalAlignment(g174,g176)
    c: InternalAlignment(g175,g176)
    c: InternalAlignment(g177,g176)
    c: InternalAlignment(g178,g176)
    c: Weight(g179) = 1
    c: Equal(g179,g180)
    c: Equal(g179,g181)
    c: InternalAlignment(g179,g182)
    c: InternalAlignment(g180,g182)
    c: InternalAlignment(g181,g182)
    c: InternalAlignment(g183,g182)
    c: InternalAlignment(g184,g182)
    c: Weight(g185) = 1
    c: Equal(g185,g186)
    c: Equal(g185,g187)
    c: InternalAlignment(g185,g188)
    c: InternalAlignment(g186,g188)
    c: InternalAlignment(g187,g188)
    c: InternalAlignment(g189,g188)
    c: InternalAlignment(g190,g188)
    c: Weight(g191) = 1
    c: Equal(g191,g192)
    c: Equal(g191,g193)
    c: InternalAlignment(g191,g194)
    c: InternalAlignment(g192,g194)
    c: InternalAlignment(g193,g194)
    c: InternalAlignment(g195,g194)
    c: InternalAlignment(g196,g194)
    c: Block(g194)
    c: Block(g188)
    c: Block(g182)
    c: Block(g176)
    c: Coincident(g197,g194)
    c: Coincident(g197,g188)
    c: Horizontal(g197)
    c: Coincident(g198,g188)
    c: Coincident(g198,g19)
    c: Vertical(g198)
    c: Coincident(g199,g25)
    c: Coincident(g199,g182)
    c: Vertical(g199)
    c: Coincident(g200,g182)
    c: Coincident(g200,g176)
    c: Horizontal(g200)
    c: Coincident(g201,g176)
    c: Coincident(g201,g25)
    c: Coincident(g202,g19)
    c: Weight(g203) = 1
    c: Equal(g203,g204)
    c: Equal(g203,g205)
    c: InternalAlignment(g203,g206)
    c: InternalAlignment(g204,g206)
    c: InternalAlignment(g205,g206)
    c: InternalAlignment(g207,g206)
    c: InternalAlignment(g208,g206)
    c: Weight(g209) = 1
    c: Equal(g209,g210)
    c: Equal(g209,g211)
    c: InternalAlignment(g209,g212)
    c: InternalAlignment(g210,g212)
    c: InternalAlignment(g211,g212)
    c: InternalAlignment(g213,g212)
    c: InternalAlignment(g214,g212)
    c: Block(g212)
    c: Block(g206)
    c: Coincident(g215,g212)
    c: Coincident(g215,g43)
    c: Coincident(g216,g43)
    c: Coincident(g216,g206)
    c: Coincident(g217,g206)
    c: Coincident(g217,g212)
    c: Vertical(g217)
    c: Weight(g218) = 1
    c: Equal(g218,g219)
    c: Equal(g218,g220)
    c: InternalAlignment(g218,g221)
    c: InternalAlignment(g219,g221)
    c: InternalAlignment(g220,g221)
    c: InternalAlignment(g222,g221)
    c: InternalAlignment(g223,g221)
    c: Weight(g224) = 1
    c: Equal(g224,g225)
    c: Equal(g224,g226)
    c: InternalAlignment(g224,g227)
    c: InternalAlignment(g225,g227)
    c: InternalAlignment(g226,g227)
    c: InternalAlignment(g228,g227)
    c: InternalAlignment(g229,g227)
    c: Block(g227)
    c: Block(g221)
    c: Coincident(g230,g221)
    c: Coincident(g230,g49)
    c: Coincident(g231,g49)
    c: Coincident(g231,g227)
    c: Coincident(g232,g227)
    c: Coincident(g232,g221)
    c: Vertical(g232)
    c: Horizontal(g233)
    c: Block(g233)
    c: Vertical(g234)
    c: Block(g234)
    c: Block(g235)
    c: Weight(g236) = 1
    c: Equal(g236,g237)
    c: Equal(g236,g238)
    c: InternalAlignment(g236,g239)
    c: InternalAlignment(g237,g239)
    c: InternalAlignment(g238,g239)
    c: InternalAlignment(g240,g239)
    c: InternalAlignment(g241,g239)
    c: Weight(g242) = 1
    c: Equal(g242,g243)
    c: Equal(g242,g244)
    c: InternalAlignment(g242,g245)
    c: InternalAlignment(g243,g245)
    c: InternalAlignment(g244,g245)
    c: InternalAlignment(g246,g245)
    c: InternalAlignment(g247,g245)
    c: Weight(g248) = 1
    c: Equal(g248,g249)
    c: Equal(g248,g250)
    c: InternalAlignment(g248,g251)
    c: InternalAlignment(g249,g251)
    c: InternalAlignment(g250,g251)
    c: InternalAlignment(g252,g251)
    c: InternalAlignment(g253,g251)
    c: Weight(g254) = 1
    c: Equal(g254,g255)
    c: Equal(g254,g256)
    c: InternalAlignment(g254,g257)
    c: InternalAlignment(g255,g257)
    c: InternalAlignment(g256,g257)
    c: InternalAlignment(g258,g257)
    c: InternalAlignment(g259,g257)
    c: Block(g239)
    c: Block(g245)
    c: Block(g251)
    c: Block(g257)
    c: Coincident(g260,g245)
    c: Coincident(g260,g239)
    c: Horizontal(g260)
    c: Block(g202)
    c: Weight(g261) = 1
    c: Equal(g261,g262)
    c: Equal(g261,g263)
    c: InternalAlignment(g261,g264)
    c: InternalAlignment(g262,g264)
    c: InternalAlignment(g263,g264)
    c: InternalAlignment(g265,g264)
    c: InternalAlignment(g266,g264)
    c: Weight(g267) = 1
    c: Equal(g267,g268)
    c: Equal(g267,g269)
    c: InternalAlignment(g267,g270)
    c: InternalAlignment(g268,g270)
    c: InternalAlignment(g269,g270)
    c: InternalAlignment(g271,g270)
    c: InternalAlignment(g272,g270)
    c: Weight(g273) = 1
    c: Equal(g273,g274)
    c: Equal(g273,g275)
    c: InternalAlignment(g273,g276)
    c: InternalAlignment(g274,g276)
    c: InternalAlignment(g275,g276)
    c: InternalAlignment(g277,g276)
    c: InternalAlignment(g278,g276)
    c: Weight(g279) = 1
    c: Equal(g279,g280)
    c: Equal(g279,g281)
    c: InternalAlignment(g279,g282)
    c: InternalAlignment(g280,g282)
    c: InternalAlignment(g281,g282)
    c: InternalAlignment(g283,g282)
    c: InternalAlignment(g284,g282)
    c: Block(g264)
    c: Block(g270)
    c: Block(g276)
    c: Block(g282)
    c: Coincident(g285,g276)
    c: Coincident(g285,g282)
    c: Horizontal(g285)
    c: Coincident(g286,g282)
    c: Coincident(g286,g264)
    c: Vertical(g286)
    c: Coincident(g287,g264)
    c: Coincident(g287,g270)
    c: Coincident(g288,g270)
    c: Coincident(g288,g276)
    c: Vertical(g288)
    c: Weight(g289) = 1
    c: Equal(g289,g290)
    c: Equal(g289,g291)
    c: InternalAlignment(g289,g292)
    c: InternalAlignment(g290,g292)
    c: InternalAlignment(g291,g292)
    c: InternalAlignment(g293,g292)
    c: InternalAlignment(g294,g292)
    c: Weight(g295) = 1
    c: Equal(g295,g296)
    c: Equal(g295,g297)
    c: InternalAlignment(g295,g298)
    c: InternalAlignment(g296,g298)
    c: InternalAlignment(g297,g298)
    c: InternalAlignment(g299,g298)
    c: InternalAlignment(g300,g298)
    c: Weight(g301) = 1
    c: Equal(g301,g302)
    c: Equal(g301,g303)
    c: InternalAlignment(g301,g304)
    c: InternalAlignment(g302,g304)
    c: InternalAlignment(g303,g304)
    c: InternalAlignment(g305,g304)
    c: InternalAlignment(g306,g304)
    c: Block(g304)
    c: Block(g298)
    c: Block(g292)
    c: Coincident(g307,g298)
    c: Coincident(g307,g292)
    c: Coincident(g308,g292)
    c: Coincident(g308,g304)
    c: Vertical(g308)
    c: Coincident(g309,g304)
    c: Coincident(g309,g298)
    c: Horizontal(g309)
FEATURE [Sketcher::SketchObject] Sketch001
  FullyConstrained = true
  MapMode = 4
  Placement = pos=(0,0,0) rot=(0.57735,0.57735,0.57735;2.0944rad)
  Support = -> [Sketch]
  sketch-geometry (46):
    g0: BSplineCurve PolesCount=3 KnotsCount=2 Degree=2 IsPeriodic=0
    g1: ArcOfCircle CenterX=73.1223 CenterY=-32.291 CenterZ=0 NormalX=0 NormalY=0 NormalZ=1 AngleXU=0 Radius=13 StartAngle=5.92268 EndAngle=9.06428
    g2: ArcOfCircle CenterX=66.7816 CenterY=-49.1439 CenterZ=0 NormalX=0 NormalY=0 NormalZ=1 AngleXU=0 Radius=13 StartAngle=2.78068 EndAngle=5.92131
    g3: ArcOfCircle CenterX=55.9263 CenterY=-78.1807 CenterZ=0 NormalX=0 NormalY=0 NormalZ=1 AngleXU=0 Radius=13 StartAngle=5.92268 EndAngle=9.06428
    g4: ArcOfCircle CenterX=49.5884 CenterY=-95.0342 CenterZ=0 NormalX=0 NormalY=0 NormalZ=1 AngleXU=0 Radius=13 StartAngle=2.78068 EndAngle=5.92131
    g5: ArcOfCircle CenterX=38.7206 CenterY=-124.067 CenterZ=0 NormalX=0 NormalY=0 NormalZ=1 AngleXU=0 Radius=13 StartAngle=5.92268 EndAngle=9.06428
    g6: ArcOfCircle CenterX=32.3875 CenterY=-140.92 CenterZ=0 NormalX=0 NormalY=0 NormalZ=1 AngleXU=0 Radius=13 StartAngle=2.78068 EndAngle=5.92131
    g7: ArcOfCircle CenterX=21.4715 CenterY=-169.934 CenterZ=0 NormalX=0 NormalY=0 NormalZ=1 AngleXU=0 Radius=13 StartAngle=5.92268 EndAngle=9.06428
    g8: ArcOfCircle CenterX=15.1336 CenterY=-186.787 CenterZ=0 NormalX=0 NormalY=0 NormalZ=1 AngleXU=0 Radius=13 StartAngle=2.78068 EndAngle=5.92131
    g9-g12: Circle x4 (B-spline internal-alignment scaffolding for g13; pole/knot coordinates omitted)
    g13: BSplineCurve PolesCount=4 KnotsCount=2 Degree=3 IsPeriodic=0
    g14: GeomPoint X=28.8094 Y=-19.0875 Z=0
    g15: GeomPoint X=47.0443 Y=-50.4712 Z=0
    g16: Circle CenterX=53.5586 CenterY=-23.2695 CenterZ=0 NormalX=0 NormalY=0 NormalZ=1 AngleXU=0 Radius=3.24518
    g17: Circle CenterX=-195.441 CenterY=-127.082 CenterZ=0 NormalX=0 NormalY=0 NormalZ=1 AngleXU=0 Radius=1
    g18: Circle CenterX=-8.24091 CenterY=-197.481 CenterZ=0 NormalX=0 NormalY=0 NormalZ=1 AngleXU=0 Radius=1
    g19: Circle CenterX=12.8789 CenterY=-141.321 CenterZ=0 NormalX=0 NormalY=0 NormalZ=1 AngleXU=0 Radius=1
    g20: BSplineCurve PolesCount=3 KnotsCount=2 Degree=2 IsPeriodic=0
    g21: GeomPoint X=-195.441 Y=-127.082 Z=0
    g22: GeomPoint X=12.8789 Y=-141.321 Z=0
    g23: Circle CenterX=-12.8016 CenterY=-179.036 CenterZ=0 NormalX=0 NormalY=0 NormalZ=1 AngleXU=0 Radius=10.5072
    g24: Circle CenterX=0.933922 CenterY=-166.43 CenterZ=0 NormalX=0 NormalY=0 NormalZ=1 AngleXU=0 Radius=3.26661
    g25: Circle CenterX=-33.5518 CenterY=-176.44 CenterZ=0 NormalX=0 NormalY=0 NormalZ=1 AngleXU=0 Radius=5.64388
    g26: Circle CenterX=-47.2366 CenterY=-173.859 CenterZ=0 NormalX=0 NormalY=0 NormalZ=1 AngleXU=0 Radius=3.01653
    g27: Circle CenterX=-56.2595 CenterY=-171.456 CenterZ=0 NormalX=0 NormalY=0 NormalZ=1 AngleXU=0 Radius=2.12826
    g28: ArcOfCircle CenterX=51.2151 CenterY=-198.473 CenterZ=0 NormalX=0 NormalY=0 NormalZ=1 AngleXU=0 Radius=20 StartAngle=2.78189 EndAngle=4.35269
    g29: LineSegment StartX=32.4951 StartY=-191.433 StartZ=0 EndX=94.6578 EndY=-26.1352 EndZ=0
    g30: LineSegment StartX=43.1192 StartY=-220.001 StartZ=0 EndX=-196.497 EndY=-129.89 EndZ=0
    g31: LineSegment StartX=43.1192 StartY=-220.001 StartZ=0 EndX=44.1752 EndY=-217.193 EndZ=0
    g32: LineSegment StartX=117.223 StartY=-19.0875 StartZ=0 EndX=117.223 EndY=-16.0875 EndZ=0
    g33: LineSegment StartX=117.223 StartY=-16.0875 StartZ=0 EndX=17.2232 EndY=-16.0875 EndZ=0
    g34: LineSegment StartX=17.2232 StartY=-16.0875 StartZ=0 EndX=17.2232 EndY=-19.0875 EndZ=0
    g35: LineSegment StartX=28.8094 StartY=-19.0875 StartZ=0 EndX=17.2232 EndY=-19.0875 EndZ=0
    g36: LineSegment StartX=47.0443 StartY=-50.4712 StartZ=0 EndX=12.8789 EndY=-141.321 EndZ=0
    g37: LineSegment StartX=-195.441 StartY=-127.082 StartZ=0 EndX=-196.497 EndY=-129.89 EndZ=0
    g38: LineSegment StartX=85.2866 StartY=-36.8766 StartZ=0 EndX=78.9396 EndY=-53.7463 EndZ=0
    g39: LineSegment StartX=60.9579 StartY=-27.7053 StartZ=0 EndX=54.6191 EndY=-44.5532 EndZ=0
    g40: LineSegment StartX=68.0907 StartY=-82.7664 StartZ=0 EndX=61.7465 EndY=-99.6365 EndZ=0
    g41: LineSegment StartX=43.7619 StartY=-73.595 StartZ=0 EndX=37.426 EndY=-90.4435 EndZ=0
    g42: LineSegment StartX=50.885 StartY=-128.652 StartZ=0 EndX=44.5456 EndY=-145.522 EndZ=0
    g43: LineSegment StartX=26.5562 StartY=-119.481 StartZ=0 EndX=20.2251 EndY=-136.329 EndZ=0
    g44: LineSegment StartX=9.3071 StartY=-165.349 StartZ=0 EndX=2.97115 EndY=-182.197 EndZ=0
    g45: LineSegment StartX=33.6358 StartY=-174.52 StartZ=0 EndX=27.2917 EndY=-191.39 EndZ=0
  constraints (71):
    c: Block(g0)
    c: Block(g1)
    c: Block(g2)
    c: Block(g4)
    c: Block(g3)
    c: Block(g6)
    c: Block(g5)
    c: Block(g8)
    c: Block(g7)
    c: Weight(g9) = 1
    c: Equal(g9,g10)
    c: Equal(g9,g11)
    c: Equal(g9,g12)
    c: InternalAlignment(g9-g12 -> g13) x4
    c: InternalAlignment(g14,g13)
    c: InternalAlignment(g15,g13)
    c: Block(g16)
    c: Weight(g17) = 1
    c: Equal(g17,g18)
    c: Equal(g17,g19)
    c: InternalAlignment(g17,g20)
    c: InternalAlignment(g18,g20)
    c: InternalAlignment(g19,g20)
    c: InternalAlignment(g21,g20)
    c: InternalAlignment(g22,g20)
    c: Block(g20)
    c: Block(g23)
    c: Block(g24)
    c: Block(g25)
    c: Block(g26)
    c: Block(g27)
    c: Block(g28)
    c: Coincident(g29,g28)
    c: Coincident(g29,g0)
    c: Block(g13)
    c: Coincident(g31,g30)
    c: Coincident(g31,g28)
    c: Block(g31)
    c: Coincident(g32,g0)
    c: Vertical(g32)
    c: Coincident(g33,g32)
    c: Horizontal(g33)
    c: Coincident(g34,g33)
    c: Vertical(g34)
    c: Block(g33)
    c: Coincident(g35,g13)
    c: Coincident(g35,g34)
    c: Horizontal(g35)
    c: Coincident(g36,g13)
    c: Coincident(g36,g20)
    c: Coincident(g37,g20)
    c: Coincident(g37,g30)
    c: Block(g30)
    c: Coincident(g38,g1)
    c: Coincident(g38,g2)
    c: Coincident(g39,g1)
    c: Coincident(g39,g2)
    c: Coincident(g40,g3)
    c: Coincident(g40,g4)
    c: Coincident(g41,g3)
    c: Coincident(g41,g4)
    c: Coincident(g42,g5)
    c: Coincident(g42,g6)
    c: Coincident(g43,g5)
    c: Coincident(g43,g6)
    c: Coincident(g44,g7)
    c: Coincident(g44,g8)
    c: Coincident(g45,g7)
    c: Coincident(g45,g8)
    c: Distance(g30) = 256
    c: Distance(g33) = 100
FEATURE [Part::Extrusion] Extrude002
  Base = -> Sketch001
  Dir = (1,0,0)
  DirMode = 2
  FaceMakerClass = Part::FaceMakerBullseye
  LengthFwd = 8
  LengthRev = 0
  Solid = true
  Symmetric = false
FEATURE [Sketcher::SketchObject] Sketch002
  FullyConstrained = true
  sketch-geometry (20):
    g0: LineSegment StartX=-2.77179 StartY=-200.304 StartZ=0 EndX=5.22821 EndY=-200.304 EndZ=0
    g1: LineSegment StartX=5.22821 StartY=-200.304 StartZ=0 EndX=5.22821 EndY=-197.304 EndZ=0
    g2: LineSegment StartX=-2.77179 StartY=-200.304 StartZ=0 EndX=-2.77179 EndY=-197.304 EndZ=0
    g3: LineSegment StartX=5.22821 StartY=-197.304 StartZ=0 EndX=8.22821 EndY=-197.304 EndZ=0
    g4: LineSegment StartX=-2.77179 StartY=-197.304 StartZ=0 EndX=-5.77179 EndY=-197.304 EndZ=0
    g5: LineSegment StartX=19.2282 StartY=-203.304 StartZ=0 EndX=19.2282 EndY=-206.304 EndZ=0
    g6: LineSegment StartX=-16.7718 StartY=-203.304 StartZ=0 EndX=-16.7718 EndY=-206.304 EndZ=0
    g7: LineSegment StartX=-16.7718 StartY=-206.304 StartZ=0 EndX=19.2282 EndY=-206.304 EndZ=0
    g8: Circle CenterX=-16.7718 CenterY=-203.304 CenterZ=0 NormalX=0 NormalY=0 NormalZ=1 AngleXU=0 Radius=1
    g9: Circle CenterX=-5.77179 CenterY=-203.304 CenterZ=0 NormalX=0 NormalY=0 NormalZ=1 AngleXU=0 Radius=1
    g10: Circle CenterX=-5.77179 CenterY=-197.304 CenterZ=0 NormalX=0 NormalY=0 NormalZ=1 AngleXU=0 Radius=1
    g11: BSplineCurve PolesCount=3 KnotsCount=2 Degree=2 IsPeriodic=0
    g12: GeomPoint X=-16.7718 Y=-203.304 Z=0
    g13: GeomPoint X=-5.77179 Y=-197.304 Z=0
    g14: Circle CenterX=19.2282 CenterY=-203.304 CenterZ=0 NormalX=0 NormalY=0 NormalZ=1 AngleXU=0 Radius=1
    g15: Circle CenterX=8.22821 CenterY=-203.304 CenterZ=0 NormalX=0 NormalY=0 NormalZ=1 AngleXU=0 Radius=1
    g16: Circle CenterX=8.22821 CenterY=-197.304 CenterZ=0 NormalX=0 NormalY=0 NormalZ=1 AngleXU=0 Radius=1
    g17: BSplineCurve PolesCount=3 KnotsCount=2 Degree=2 IsPeriodic=0
    g18: GeomPoint X=19.2282 Y=-203.304 Z=0
    g19: GeomPoint X=8.22821 Y=-197.304 Z=0
  constraints (41):
    c: Horizontal(g0)
    c: Distance(g0) = 8
    c: Coincident(g1,g0)
    c: Vertical(g1)
    c: Distance(g1) = 3
    c: Coincident(g2,g0)
    c: Vertical(g2)
    c: Distance(g2) = 3
    c: Coincident(g3,g1)
    c: Horizontal(g3)
    c: Distance(g3) = 3
    c: Coincident(g4,g2)
    c: Horizontal(g4)
    c: Distance(g4) = 3
    c: Vertical(g5)
    c: Vertical(g6)
    c: Coincident(g7,g6)
    c: Coincident(g7,g5)
    c: Weight(g8) = 1
    c: Equal(g8,g9)
    c: Equal(g8,g10)
    c: Coincident(g11,g4)
    c: InternalAlignment(g8,g11)
    c: InternalAlignment(g9,g11)
    c: InternalAlignment(g10,g11)
    c: InternalAlignment(g12,g11)
    c: InternalAlignment(g13,g11)
    c: Coincident(g17,g5)
    c: Weight(g14) = 1
    c: Equal(g14,g15)
    c: Equal(g14,g16)
    c: Coincident(g17,g3)
    c: InternalAlignment(g14,g17)
    c: InternalAlignment(g15,g17)
    c: InternalAlignment(g16,g17)
    c: InternalAlignment(g18,g17)
    c: InternalAlignment(g19,g17)
    c: Block(g7)
    c: Block(g17)
    c: Block(g11)
    c: Block(g6)
FEATURE [Part::Extrusion] Extrude003
  Base = -> Sketch002
  Dir = (0,0,1)
  DirMode = 2
  FaceMakerClass = Part::FaceMakerBullseye
  LengthFwd = 260
  LengthRev = 0
  Solid = true
  Symmetric = false
FEATURE [Part::Extrusion] Extrude
  Base = -> Sketch
  Dir = (0,0,1)
  DirMode = 2
  FaceMakerClass = Part::FaceMakerBullseye
  LengthFwd = 14
  LengthRev = 0
  Solid = true
  Symmetric = false
